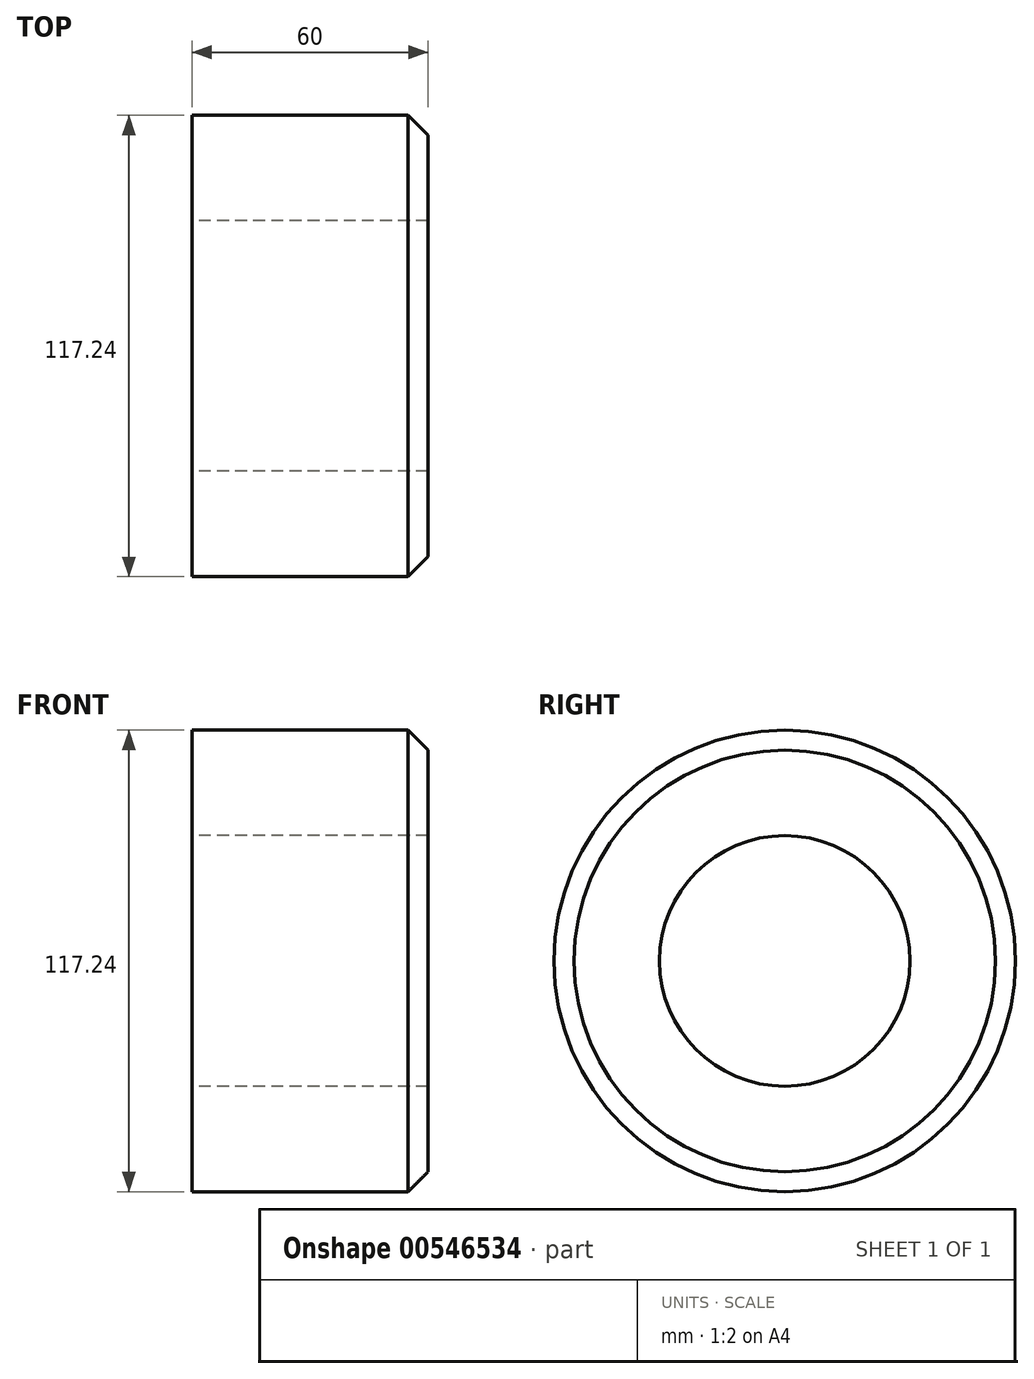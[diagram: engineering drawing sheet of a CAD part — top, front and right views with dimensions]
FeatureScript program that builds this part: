
annotation { "Feature Type Name" : "Feature", "Feature Type Description" : "" }
export const myFeature = defineFeature(function(context is Context, id is Id, definition is map)
    precondition{}
    {
        {
            var Q0;
            Q0=qCreatedBy(makeId("Right.planeOp"),FACE);
            var sketch = newSketch(context, id + "F0", { "sketchPlane" : qUnion([Q0])});
            skCircle(sketch, "E0", {"center": v(0, 0) * mm, "radius": 58.62 * mm});
            skCircle(sketch, "E1", {"center": v(0, 0) * mm, "radius": 31.84 * mm});
            skSolve(sketch);
        }
        {
            var Q0;
            Q0=makeQuery(id+"F0.imprint","IMPRINT",FACE,{"disambiguationData":[TD([[makeQuery(id+"F0.imprint","IMPRINT",EDGE,{"derivedFrom":sQuery(id+"F0.wireOp",EDGE,"E0")}),1.0]])]});
            extrude(context, id + "F1", {"entities" : qUnion([Q0]), "depth" : 60 * mm, "offsetDistance" : 25.4 * mm});
        }
        {
            var Q0;
            Q0=makeQuery(id+"F1.opExtrude","CAP_EDGE",EDGE,{"disambiguationData":[OSD([sQuery(id+"F0.wireOp",EDGE,"E0")])],"isStart":false});
            chamfer(context, id + "F2", {"entities" : qUnion([Q0]), "width" : 5.08 * mm, "tangentPropagation" : true});
        }
    });
